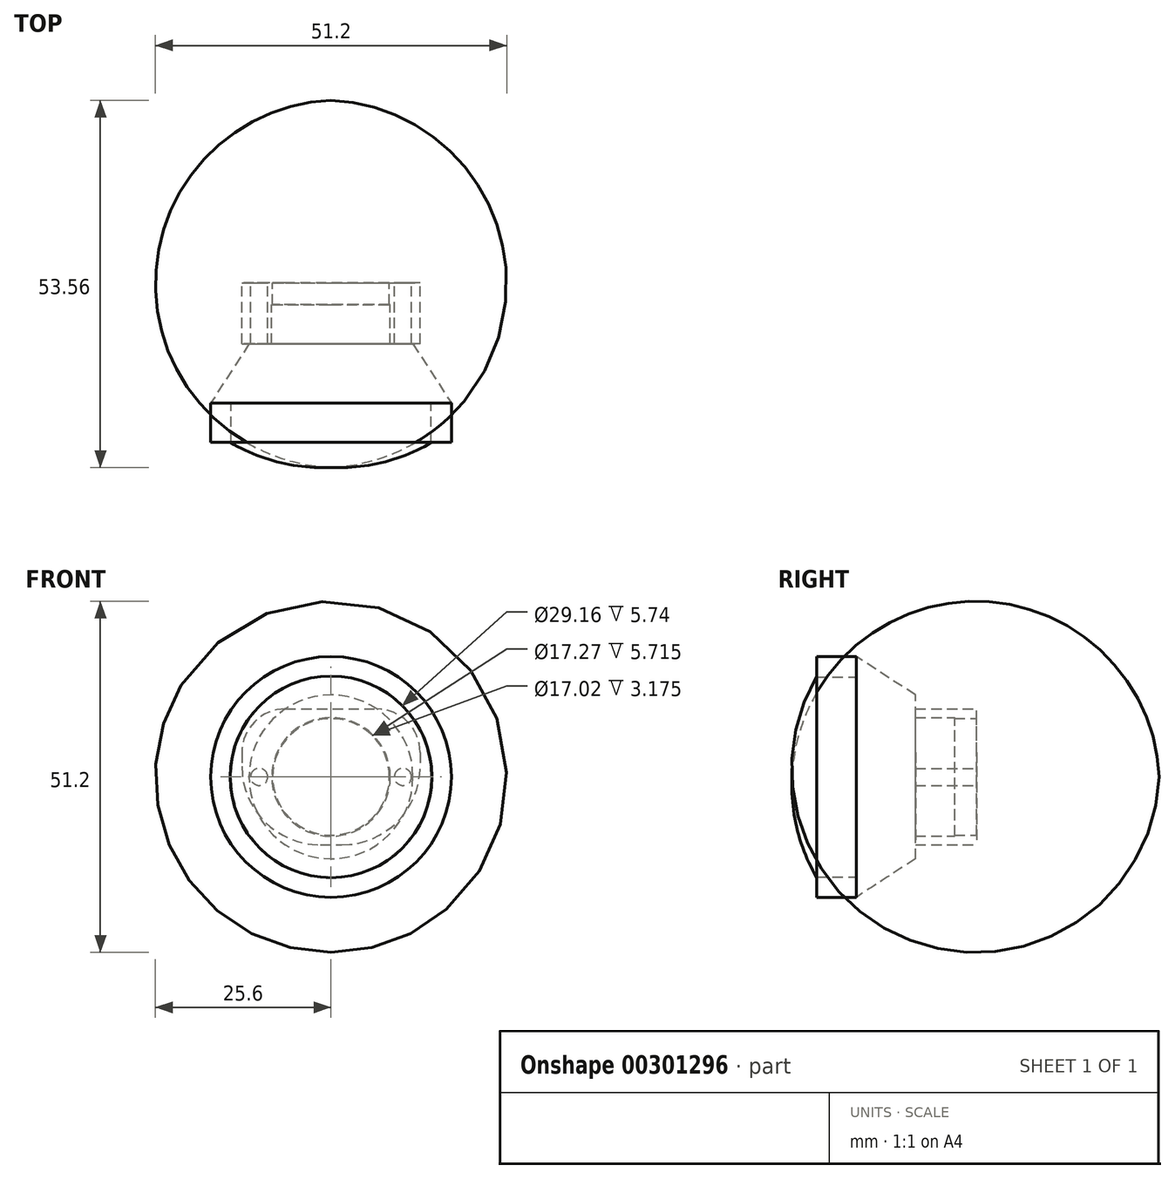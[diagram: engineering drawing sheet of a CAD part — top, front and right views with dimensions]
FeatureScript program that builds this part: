
annotation { "Feature Type Name" : "Feature", "Feature Type Description" : "" }
export const myFeature = defineFeature(function(context is Context, id is Id, definition is map)
    precondition{}
    {
        {
            var Q0;
            Q0=qCreatedBy(makeId("Front.planeOp"),FACE);
            var sketch = newSketch(context, id + "F0", { "sketchPlane" : qUnion([Q0])});
            skPoint(sketch, "E0.middle", {"position": v(0, 0) * mm});
            skCircle(sketch, "E1", {"center": v(0, 0) * mm, "radius": 8.5 * mm});
            skCircle(sketch, "E2", {"center": v(-10.48, 0) * mm, "radius": 1.24 * mm});
            skCircle(sketch, "E3", {"center": v(10.48, 0) * mm, "radius": 1.24 * mm});
            skLineSegment(sketch, "E4.bottom", {"start": v(-6.64, 9.9) * mm, "end": v(6.64, 9.9) * mm});
            skLineSegment(sketch, "E4.top", {"start": v(-1.56, -9.9) * mm, "end": v(1.56, -9.9) * mm});
            skLineSegment(sketch, "E4.left", {"start": v(-13, 3.56) * mm, "end": v(-13, 1.52) * mm});
            skLineSegment(sketch, "E4.right", {"start": v(13, 3.56) * mm, "end": v(13, 1.52) * mm});
            skPoint(sketch, "E5.visualSharp", {"position": v(-13, 9.9) * mm});
            skArc(sketch, "E5.filletArc", {"start": v(-6.64, 9.9) * mm, "mid": v(-11.13, 8.05) * mm, "end": v(-13, 3.56) * mm});
            skPoint(sketch, "E6.visualSharp", {"position": v(13, 9.9) * mm});
            skArc(sketch, "E6.filletArc", {"start": v(13, 3.56) * mm, "mid": v(11.13, 8.05) * mm, "end": v(6.64, 9.9) * mm});
            skPoint(sketch, "E7.visualSharp", {"position": v(13, -9.9) * mm});
            skArc(sketch, "E7.filletArc", {"start": v(1.56, -9.9) * mm, "mid": v(9.64, -6.56) * mm, "end": v(13, 1.52) * mm});
            skPoint(sketch, "E8.visualSharp", {"position": v(-13, -9.9) * mm});
            skArc(sketch, "E8.filletArc", {"start": v(-13, 1.52) * mm, "mid": v(-9.64, -6.56) * mm, "end": v(-1.56, -9.9) * mm});
            skCircle(sketch, "E9", {"center": v(0, 0) * mm, "radius": 8.64 * mm});
            skSolve(sketch);
        }
        {
            var Q0;
            Q0=makeQuery(id+"F0.imprint","IMPRINT",FACE,{"disambiguationData":[TD([[makeQuery(id+"F0.imprint","IMPRINT",EDGE,{"derivedFrom":sQuery(id+"F0.wireOp",EDGE,"E2")}),-1.0]])]});
            extrude(context, id + "F1", {"entities" : qUnion([Q0]), "depth" : 8.9 * mm});
        }
        {
            var Q0;
            Q0=makeQuery(id+"F0.imprint","IMPRINT",FACE,{"disambiguationData":[TD([[makeQuery(id+"F0.imprint","IMPRINT",EDGE,{"derivedFrom":sQuery(id+"F0.wireOp",EDGE,"E1")}),-1.0]])]});
            extrude(context, id + "F2", {"entities" : qUnion([Q0]), "operationType" : NewBodyOperationType.ADD, "depth" : 3.17 * mm});
        }
        {
            var Q0;
            Q0=makeQuery(id+"F1.opExtrude","CAP_FACE",FACE,{"disambiguationData":[OSD([sQuery(id+"F0.wireOp",EDGE,"E2"),sQuery(id+"F0.wireOp",EDGE,"E3"),sQuery(id+"F0.wireOp",EDGE,"E4.bottom"),sQuery(id+"F0.wireOp",EDGE,"E4.top"),sQuery(id+"F0.wireOp",EDGE,"E4.left"),sQuery(id+"F0.wireOp",EDGE,"E4.right"),sQuery(id+"F0.wireOp",EDGE,"E5.filletArc"),sQuery(id+"F0.wireOp",EDGE,"E6.filletArc"),sQuery(id+"F0.wireOp",EDGE,"E7.filletArc"),sQuery(id+"F0.wireOp",EDGE,"E8.filletArc"),sQuery(id+"F0.wireOp",EDGE,"E9")])],"isStart":false});
            var sketch = newSketch(context, id + "F3", { "sketchPlane" : qUnion([Q0])});
            skCircle(sketch, "E10", {"center": v(0, 0) * mm, "radius": 11.94 * mm});
            skSolve(sketch);
        }
        {
            var Q0;
            Q0 = qSketchRegion(id + "F3", true);
            var Q1;
            Q1=sQuery(id+"F3.wireOp",EDGE,"E10");
            extrude(context, id + "F4", {"entities" : qUnion([Q0]), "surfaceEntities" : qUnion([Q1]), "depth" : 8.64 * mm, "hasDraft" : true, "draftAngle" : 33 * degree});
        }
        {
            var Q0;
            Q0=makeQuery(id+"F4.opExtrude","CAP_FACE",FACE,{"disambiguationData":[OSD([sQuery(id+"F3.wireOp",EDGE,"E10")])],"isStart":false});
            var sketch = newSketch(context, id + "F5", { "sketchPlane" : qUnion([Q0])});
            skCircle(sketch, "E11", {"center": v(0, 0) * mm, "radius": 17.55 * mm});
            skCircle(sketch, "E12", {"center": v(0, 0) * mm, "radius": 14.58 * mm});
            skSolve(sketch);
        }
        {
            var Q0;
            Q0 = qSketchRegion(id + "F5", true);
            extrude(context, id + "F6", {"entities" : qUnion([Q0]), "operationType" : NewBodyOperationType.ADD, "depth" : 5.74 * mm});
        }
        {
            var Q0;
            Q0=qCreatedBy(makeId("Right.planeOp"),FACE);
            var sketch = newSketch(context, id + "F7", { "sketchPlane" : qUnion([Q0])});
            skArc(sketch, "E13", {"start": v(-26.9, 0) * mm, "mid": v(-26.14, -7.61) * mm, "end": v(-23.27, -14.7) * mm});
            skLineSegment(sketch, "E14", {"start": v(-23.27, -14.7) * mm, "end": v(-23.27, 0) * mm});
            skLineSegment(sketch, "E15", {"start": v(-23.27, 0) * mm, "end": v(-26.9, 0) * mm});
            skSolve(sketch);
        }
        {
            var Q0;
            Q0=makeQuery(id+"F7.imprint","IMPRINT",FACE,{"disambiguationData":[TD([[makeQuery(id+"F7.imprint","IMPRINT",EDGE,{"derivedFrom":sQuery(id+"F7.wireOp",EDGE,"E13")}),1.0]])]});
            var Q1;
            Q1=sQuery(id+"F7.wireOp",EDGE,"E15");
            revolve(context, id + "F8", {"entities" : qUnion([Q0]), "axis" : qUnion([Q1]), "revolveType" : RevolveType.FULL});
        }
    });
